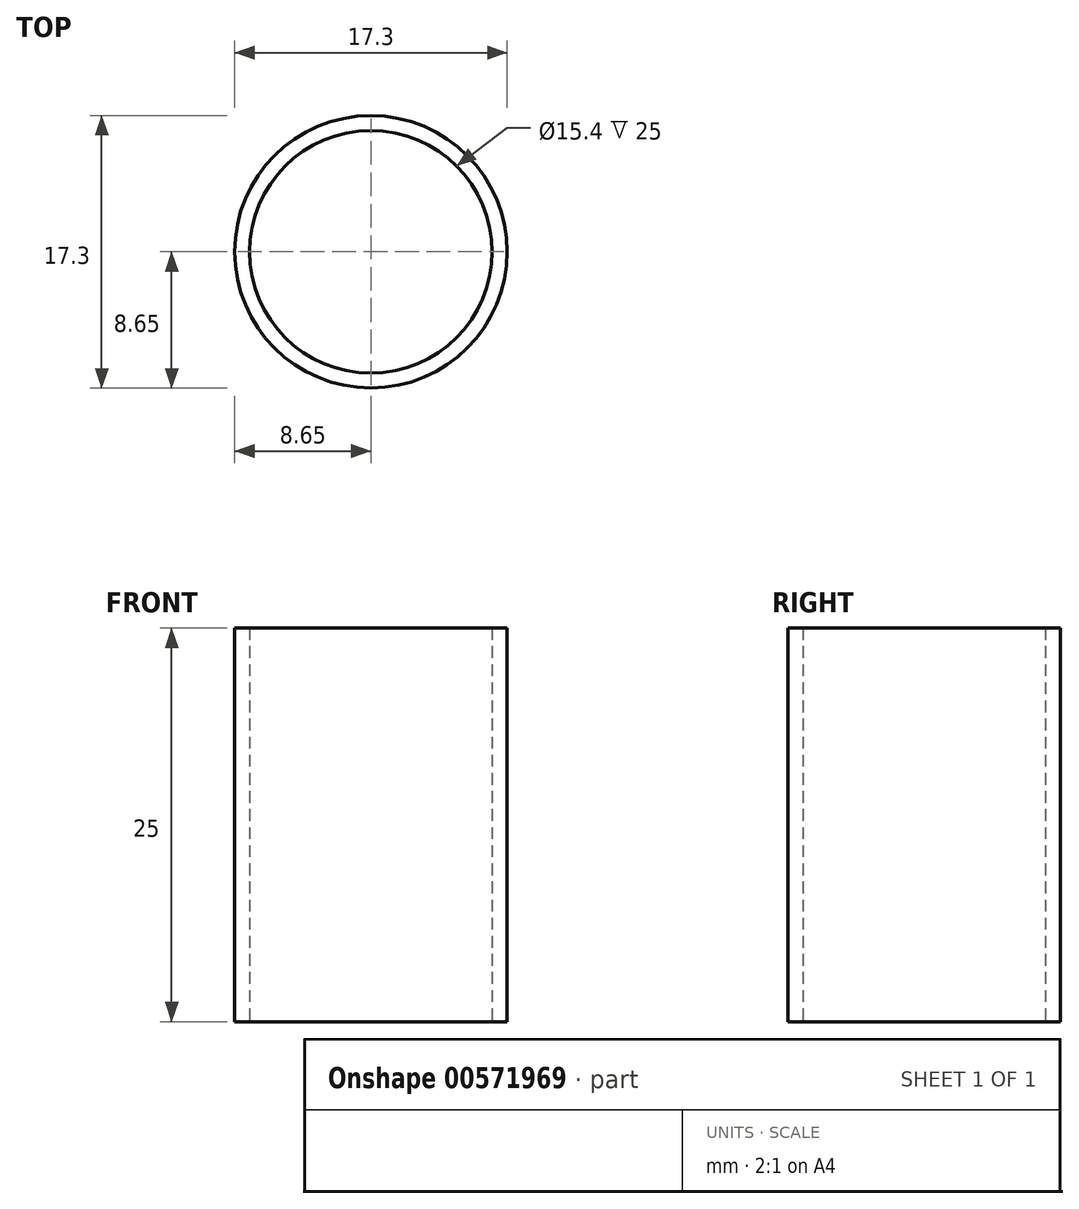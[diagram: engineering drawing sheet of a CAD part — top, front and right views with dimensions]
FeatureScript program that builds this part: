
annotation { "Feature Type Name" : "Feature", "Feature Type Description" : "" }
export const myFeature = defineFeature(function(context is Context, id is Id, definition is map)
    precondition{}
    {
        {
            var Q0;
            Q0=qCreatedBy(makeId("Top.planeOp"),FACE);
            var sketch = newSketch(context, id + "F0", { "sketchPlane" : qUnion([Q0])});
            skCircle(sketch, "E0", {"center": v(0, 0) * mm, "radius": 8.65 * mm});
            skCircle(sketch, "E1", {"center": v(0, 0) * mm, "radius": 7.7 * mm});
            skSolve(sketch);
        }
        {
            var Q0;
            Q0=makeQuery(id+"F0.imprint","IMPRINT",FACE,{"disambiguationData":[TD([[makeQuery(id+"F0.imprint","IMPRINT",EDGE,{"derivedFrom":sQuery(id+"F0.wireOp",EDGE,"E0")}),1.0]])]});
            extrude(context, id + "F1", {"entities" : qUnion([Q0]), "depth" : 25 * mm, "offsetDistance" : 25 * mm});
        }
    });
